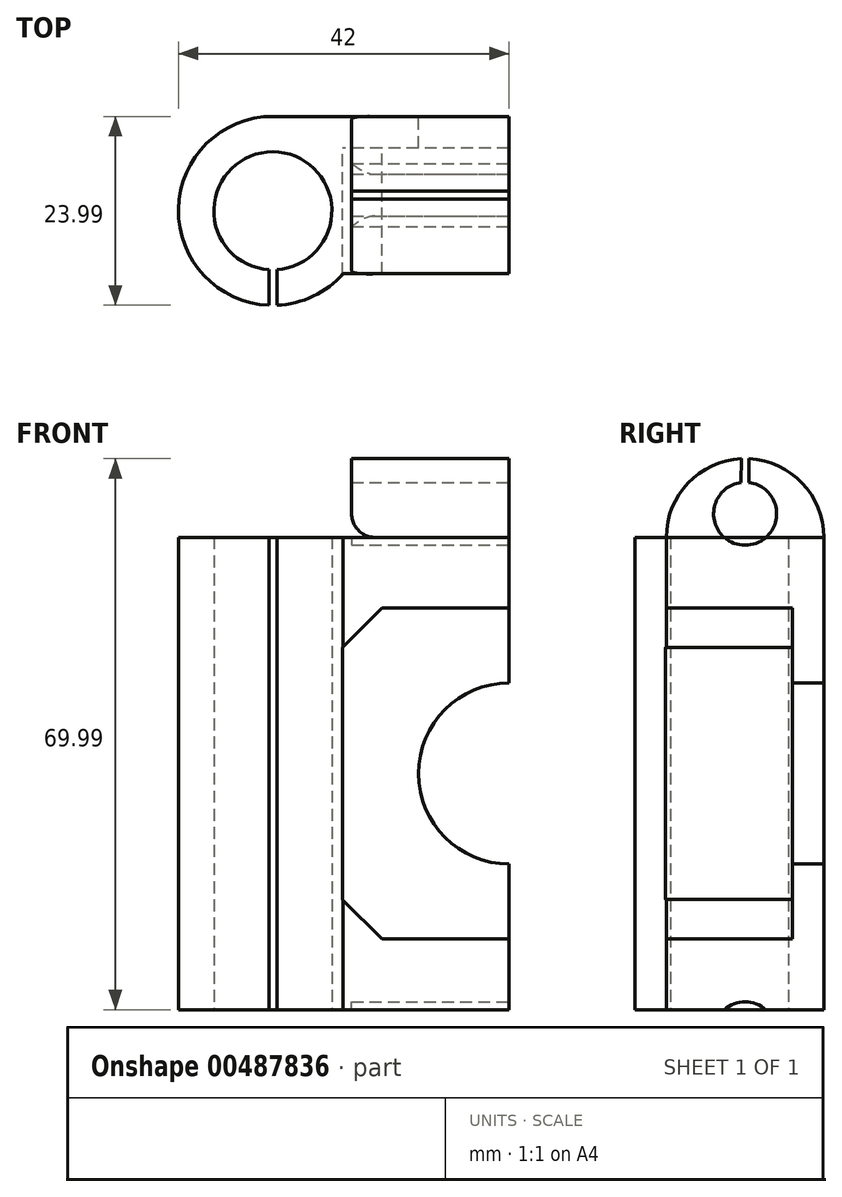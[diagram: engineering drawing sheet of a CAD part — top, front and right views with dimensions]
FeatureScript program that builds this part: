
annotation { "Feature Type Name" : "Feature", "Feature Type Description" : "" }
export const myFeature = defineFeature(function(context is Context, id is Id, definition is map)
    precondition{}
    {
        {
            var Q0;
            Q0=qCreatedBy(makeId("Top.planeOp"),FACE);
            var sketch = newSketch(context, id + "F0", { "sketchPlane" : qUnion([Q0])});
            skLineSegment(sketch, "E0.bottom", {"start": v(8.94, 0) * mm, "end": v(30, 0) * mm});
            skLineSegment(sketch, "E0.top", {"start": v(0, 20) * mm, "end": v(30, 20) * mm});
            skLineSegment(sketch, "E0.right", {"start": v(30, 0) * mm, "end": v(30, 20) * mm});
            skArc(sketch, "E1", {"start": v(0, 20) * mm, "mid": v(-10.95, 3.1) * mm, "end": v(8.94, 0) * mm});
            skCircle(sketch, "E2", {"center": v(0, 8) * mm, "radius": 7.5 * mm});
            skLineSegment(sketch, "E3", {"start": v(30, 0) * mm, "end": v(10, 0) * mm});
            skLineSegment(sketch, "E4", {"start": v(10, 0) * mm, "end": v(10, 20) * mm, "construction": true});
            skLineSegment(sketch, "E5.left", {"start": v(-0.5, -3.99) * mm, "end": v(-0.5, 0.52) * mm});
            skLineSegment(sketch, "E5.right", {"start": v(0.5, -3.99) * mm, "end": v(0.5, 0.52) * mm});
            skPoint(sketch, "E5.middle", {"position": v(0, 0) * mm});
            skPoint(sketch, "E6.orphan", {"position": v(-0.5, 4.29) * mm});
            skPoint(sketch, "E7.orphan", {"position": v(0.5, 4.29) * mm});
            skPoint(sketch, "E5.bottom.end.orphan", {"position": v(0.5, -4.29) * mm});
            skPoint(sketch, "E5.bottom.start.orphan", {"position": v(-0.5, -4.29) * mm});
            skSolve(sketch);
        }
        {
            var Q0;
            Q0=makeQuery(id+"F0.imprint","IMPRINT",FACE,{"disambiguationData":[TD([[makeQuery(id+"F0.imprint","IMPRINT",EDGE,{"derivedFrom":sQuery(id+"F0.wireOp",EDGE,"E0.bottom")}),1.0]])]});
            extrude(context, id + "F1", {"entities" : qUnion([Q0]), "depth" : 60 * mm, "offsetDistance" : 25 * mm, "symmetric" : true});
        }
        {
            var Q0;
            Q0=makeQuery(id+"F1.opExtrude","SWEPT_FACE",FACE,{"disambiguationData":[OSD([sQuery(id+"F0.wireOp",EDGE,"E0.top")])]});
            var sketch = newSketch(context, id + "F2", { "sketchPlane" : qUnion([Q0])});
            skLineSegment(sketch, "E8", {"start": v(-30, 30) * mm, "end": v(-30, 11.5) * mm});
            skLineSegment(sketch, "E9", {"start": v(-30, -30) * mm, "end": v(-30, -11.5) * mm});
            skArc(sketch, "E10", {"start": v(-30, -11.5) * mm, "mid": v(-18.5, 0) * mm, "end": v(-30, 11.5) * mm});
            skSolve(sketch);
        }
        {
            var Q0;
            {var subQ0=sQuery(id+"F2.wireOp",EDGE,"E10");Q0=makeQuery(id+"F2.imprint","IMPRINT",FACE,{"disambiguationData":[TD([[makeQuery(id+"F2.imprint","IMPRINT",EDGE,{"derivedFrom":subQ0}),1.0]])]});}
            extrude(context, id + "F3", {"entities" : qUnion([Q0]), "operationType" : NewBodyOperationType.REMOVE, "oppositeDirection" : true, "depth" : 25 * mm, "offsetDistance" : 25 * mm});
        }
        {
            var Q0;
            Q0=makeQuery(id+"F1.opExtrude","SWEPT_FACE",FACE,{"disambiguationData":[OSD([sQuery(id+"F0.wireOp",EDGE,"E0.top")])]});
            var sketch = newSketch(context, id + "F4", { "sketchPlane" : qUnion([Q0])});
            skLineSegment(sketch, "E11", {"start": v(-30, 21) * mm, "end": v(-13.85, 21) * mm});
            skLineSegment(sketch, "E12", {"start": v(-30, -21) * mm, "end": v(-13.85, -21) * mm});
            skLineSegment(sketch, "E13", {"start": v(-8.85, -16) * mm, "end": v(-8.85, 16) * mm});
            skLineSegment(sketch, "E14", {"start": v(-30, -21) * mm, "end": v(-30, 21) * mm});
            skPoint(sketch, "E15.visualSharp", {"position": v(-8.85, 21) * mm});
            skPoint(sketch, "E16.visualSharp", {"position": v(-8.85, -21) * mm});
            skLineSegment(sketch, "E17", {"start": v(-13.85, -21) * mm, "end": v(-8.85, -16) * mm});
            skLineSegment(sketch, "E18", {"start": v(-8.85, 16) * mm, "end": v(-13.85, 21) * mm});
            skLineSegment(sketch, "E19", {"start": v(-13.85, -21) * mm, "end": v(-8.85, -21) * mm, "construction": true});
            skLineSegment(sketch, "E20", {"start": v(-8.85, -16) * mm, "end": v(-8.85, -21) * mm, "construction": true});
            skLineSegment(sketch, "E21", {"start": v(-8.85, 16) * mm, "end": v(-8.85, 21) * mm, "construction": true});
            skLineSegment(sketch, "E22", {"start": v(-8.85, 21) * mm, "end": v(-13.85, 21) * mm, "construction": true});
            skSolve(sketch);
        }
        {
            var Q0;
            {var subQ3=sQuery(id+"F4.wireOp",EDGE,"E11");Q0=makeQuery(id+"F4.imprint","IMPRINT",FACE,{"disambiguationData":[TD([[makeQuery(id+"F4.imprint","IMPRINT",EDGE,{"derivedFrom":subQ3}),-1.0]])]});}
            extrude(context, id + "F5", {"entities" : qUnion([Q0]), "operationType" : NewBodyOperationType.REMOVE, "endBound" : BoundingType.THROUGH_ALL, "oppositeDirection" : true, "depth" : 10 * mm, "hasOffset" : true, "offsetDistance" : 10 * mm, "hasSecondDirection" : true, "secondDirectionOppositeDirection" : true, "secondDirectionDepth" : 4 * mm});
        }
        {
            var Q0;
            {var subQ0=sQuery(id+"F0.wireOp",EDGE,"E3");var subQ1=sQuery(id+"F0.wireOp",EDGE,"E0.right");var subQ2=sQuery(id+"F0.wireOp",EDGE,"E0.top");var subQ3=sQuery(id+"F0.wireOp",EDGE,"E0.bottom");Q0=makeQuery(id+"F3.boolean.opBoolean","SPLIT",FACE,{"disambiguationData":[TD([makeQuery(id+"F1.opExtrude","CAP_FACE",FACE,{"disambiguationData":[OSD([subQ3,subQ2,subQ1,sQuery(id+"F0.wireOp",EDGE,"E1"),sQuery(id+"F0.wireOp",EDGE,"E2"),subQ0])],"isStart":false})])],"derivedFrom":makeQuery(id+"F1.opExtrude","SWEPT_FACE",FACE,{"disambiguationData":[OSD([subQ1])]})});}
            var Q1;
            {var subQ0=sQuery(id+"F0.wireOp",EDGE,"E3");var subQ1=sQuery(id+"F0.wireOp",EDGE,"E0.right");var subQ2=sQuery(id+"F0.wireOp",EDGE,"E0.top");var subQ3=sQuery(id+"F0.wireOp",EDGE,"E0.bottom");Q1=makeQuery(id+"F3.boolean.opBoolean","SPLIT",FACE,{"disambiguationData":[TD([makeQuery(id+"F1.opExtrude","CAP_FACE",FACE,{"disambiguationData":[OSD([subQ3,subQ2,subQ1,sQuery(id+"F0.wireOp",EDGE,"E1"),sQuery(id+"F0.wireOp",EDGE,"E2"),subQ0])],"isStart":true})])],"derivedFrom":makeQuery(id+"F1.opExtrude","SWEPT_FACE",FACE,{"disambiguationData":[OSD([subQ1])]})});}
            cPlane(context, id + "F6", {"entities" : qUnion([Q0, Q1]), "cplaneType" : CPlaneType.MID_PLANE, "offset" : 25 * mm, "width" : 150 * mm, "height" : 150 * mm});
        }
        {
            var Q0;
            Q0=qCreatedBy(id+"F6.planeOp",FACE);
            var sketch = newSketch(context, id + "F7", { "sketchPlane" : qUnion([Q0])});
            skPoint(sketch, "E23", {"position": v(10, -30) * mm});
            skPoint(sketch, "E24", {"position": v(20, -30) * mm});
            skPoint(sketch, "E25", {"position": v(0, -30) * mm});
            skArc(sketch, "E26", {"start": v(20, -30) * mm, "mid": v(10, -40) * mm, "end": v(0, -30) * mm});
            skArc(sketch, "E27.MirrorCS", {"start": v(20, 30) * mm, "mid": v(10, 40) * mm, "end": v(0, 30) * mm});
            skLineSegment(sketch, "E28", {"start": v(20, 30) * mm, "end": v(0, 30) * mm});
            skLineSegment(sketch, "E29", {"start": v(20, -30) * mm, "end": v(0, -30) * mm});
            skSolve(sketch);
        }
        {
            var Q0;
            Q0=makeQuery(id+"F7.imprint","IMPRINT",FACE,{"disambiguationData":[TD([[makeQuery(id+"F7.imprint","IMPRINT",EDGE,{"derivedFrom":sQuery(id+"F7.wireOp",EDGE,"E27.MirrorCS")}),1.0]])]});
            var Q1;
            Q1=makeQuery(id+"F7.imprint","IMPRINT",FACE,{"disambiguationData":[TD([[makeQuery(id+"F7.imprint","IMPRINT",EDGE,{"derivedFrom":sQuery(id+"F7.wireOp",EDGE,"E26")}),-1.0]])]});
            extrude(context, id + "F8", {"entities" : qUnion([Q0, Q1]), "oppositeDirection" : true, "depth" : 20 * mm, "offsetDistance" : 25 * mm});
        }
        {
            var Q0;
            Q0=qCreatedBy(id+"F6.planeOp",FACE);
            var sketch = newSketch(context, id + "F9", { "sketchPlane" : qUnion([Q0])});
            skLineSegment(sketch, "E30", {"start": v(0, 0) * mm, "end": v(20, 0) * mm, "construction": true});
            skLineSegment(sketch, "E31", {"start": v(10, 0) * mm, "end": v(10, -39.9) * mm, "construction": true});
            skLineSegment(sketch, "E32", {"start": v(10, 0) * mm, "end": v(10, 40) * mm, "construction": true});
            skArc(sketch, "E33", {"start": v(9.5, 36.97) * mm, "mid": v(10, 29) * mm, "end": v(10.5, 36.97) * mm});
            skArc(sketch, "E34.MirrorC", {"start": v(9.5, -36.97) * mm, "mid": v(10, -29) * mm, "end": v(10.5, -36.97) * mm});
            skLineSegment(sketch, "E35.bottom", {"start": v(9.5, 40) * mm, "end": v(10.5, 40) * mm});
            skLineSegment(sketch, "E35.left", {"start": v(9.5, 40) * mm, "end": v(9.5, 36.97) * mm});
            skLineSegment(sketch, "E35.right", {"start": v(10.5, 40) * mm, "end": v(10.5, 36.97) * mm});
            skPoint(sketch, "E35.middle", {"position": v(10, 37) * mm});
            skPoint(sketch, "E36.orphan", {"position": v(9.5, 34) * mm});
            skPoint(sketch, "E35.top.end.orphan", {"position": v(10.5, 34) * mm});
            skLineSegment(sketch, "E37.MirrorCS", {"start": v(9.5, -40) * mm, "end": v(10.5, -40) * mm});
            skLineSegment(sketch, "E38.MirrorCS", {"start": v(10.5, -40) * mm, "end": v(10.5, -36.97) * mm});
            skLineSegment(sketch, "E39.MirrorCS", {"start": v(9.5, -40) * mm, "end": v(9.5, -36.97) * mm});
            skSolve(sketch);
        }
        {
            var Q0;
            Q0=makeQuery(id+"F9.imprint","IMPRINT",FACE,{"disambiguationData":[TD([[makeQuery(id+"F9.imprint","IMPRINT",EDGE,{"derivedFrom":sQuery(id+"F9.wireOp",EDGE,"E33")}),1.0]])]});
            var Q1;
            Q1=makeQuery(id+"F9.imprint","IMPRINT",FACE,{"disambiguationData":[TD([[makeQuery(id+"F9.imprint","IMPRINT",EDGE,{"derivedFrom":sQuery(id+"F9.wireOp",EDGE,"E34.MirrorC")}),-1.0]])]});
            var Q2;
            Q2=makeQuery(id+"F9.imprint","IMPRINT",FACE,{"disambiguationData":[TD([[makeQuery(id+"F9.imprint","IMPRINT",EDGE,{"derivedFrom":sQuery(id+"F9.wireOp",EDGE,"E35.bottom")}),-1.0]])]});
            var Q3;
            Q3=makeQuery(id+"F9.imprint","IMPRINT",FACE,{"disambiguationData":[TD([[makeQuery(id+"F9.imprint","IMPRINT",EDGE,{"derivedFrom":sQuery(id+"F9.wireOp",EDGE,"E37.MirrorCS")}),1.0]])]});
            extrude(context, id + "F10", {"entities" : qUnion([Q0, Q1, Q2, Q3]), "operationType" : NewBodyOperationType.REMOVE, "oppositeDirection" : true, "depth" : 20 * mm, "offsetDistance" : 25 * mm});
        }
        {
            var Q0;
            {var subQ0=sQuery(id+"F7.wireOp",EDGE,"E29");var subQ1=sQuery(id+"F7.wireOp",EDGE,"E26");var subQ2=makeQuery(id+"F8.opExtrude","CAP_FACE",FACE,{"disambiguationData":[OSD([subQ1,subQ0])],"isStart":false});var subQ3=sQuery(id+"F0.wireOp",EDGE,"E3");var subQ4=sQuery(id+"F0.wireOp",EDGE,"E0.bottom");var subQ5=makeQuery(id+"F1.opExtrude","CAP_FACE",FACE,{"disambiguationData":[OSD([subQ4,sQuery(id+"F0.wireOp",EDGE,"E0.top"),sQuery(id+"F0.wireOp",EDGE,"E0.right"),sQuery(id+"F0.wireOp",EDGE,"E1"),sQuery(id+"F0.wireOp",EDGE,"E2"),subQ3])],"isStart":true});Q0=makeQuery(id+"F10.boolean.opBoolean","SPLIT",EDGE,{"disambiguationData":[topologyDisambiguationEdgeConnected([subQ5,subQ2]),TD([makeQuery(id+"F1.opExtrude","SWEPT_FACE",FACE,{"disambiguationData":[OSD([subQ4,subQ3])]})])],"derivedFrom":makeQuery(id+"F8.opExtrude","CAP_EDGE",EDGE,{"disambiguationData":[OSD([subQ0])],"isStart":false})});}
            var Q1;
            {var subQ0=sQuery(id+"F7.wireOp",EDGE,"E29");var subQ1=sQuery(id+"F7.wireOp",EDGE,"E26");var subQ2=makeQuery(id+"F8.opExtrude","CAP_FACE",FACE,{"disambiguationData":[OSD([subQ1,subQ0])],"isStart":false});var subQ3=sQuery(id+"F0.wireOp",EDGE,"E0.top");var subQ5=makeQuery(id+"F1.opExtrude","CAP_FACE",FACE,{"disambiguationData":[OSD([sQuery(id+"F0.wireOp",EDGE,"E0.bottom"),subQ3,sQuery(id+"F0.wireOp",EDGE,"E0.right"),sQuery(id+"F0.wireOp",EDGE,"E1"),sQuery(id+"F0.wireOp",EDGE,"E2"),sQuery(id+"F0.wireOp",EDGE,"E3")])],"isStart":true});Q1=makeQuery(id+"F10.boolean.opBoolean","SPLIT",EDGE,{"disambiguationData":[topologyDisambiguationEdgeConnected([subQ5,subQ2]),TD([makeQuery(id+"F1.opExtrude","SWEPT_FACE",FACE,{"disambiguationData":[OSD([subQ3])]})])],"derivedFrom":makeQuery(id+"F8.opExtrude","CAP_EDGE",EDGE,{"disambiguationData":[OSD([subQ0])],"isStart":false})});}
            var Q2;
            {var subQ0=sQuery(id+"F7.wireOp",EDGE,"E28");var subQ1=sQuery(id+"F7.wireOp",EDGE,"E27.MirrorCS");var subQ2=makeQuery(id+"F8.opExtrude","CAP_FACE",FACE,{"disambiguationData":[OSD([subQ1,subQ0])],"isStart":false});var subQ4=sQuery(id+"F0.wireOp",EDGE,"E0.top");var subQ5=makeQuery(id+"F1.opExtrude","CAP_FACE",FACE,{"disambiguationData":[OSD([sQuery(id+"F0.wireOp",EDGE,"E0.bottom"),subQ4,sQuery(id+"F0.wireOp",EDGE,"E0.right"),sQuery(id+"F0.wireOp",EDGE,"E1"),sQuery(id+"F0.wireOp",EDGE,"E2"),sQuery(id+"F0.wireOp",EDGE,"E3")])],"isStart":false});Q2=makeQuery(id+"F10.boolean.opBoolean","SPLIT",EDGE,{"disambiguationData":[topologyDisambiguationEdgeConnected([subQ5,subQ2]),TD([makeQuery(id+"F1.opExtrude","SWEPT_FACE",FACE,{"disambiguationData":[OSD([subQ4])]})])],"derivedFrom":makeQuery(id+"F8.opExtrude","CAP_EDGE",EDGE,{"disambiguationData":[OSD([subQ0])],"isStart":false})});}
            var Q3;
            {var subQ0=sQuery(id+"F7.wireOp",EDGE,"E27.MirrorCS");var subQ1=sQuery(id+"F7.wireOp",EDGE,"E28");var subQ2=makeQuery(id+"F8.opExtrude","CAP_FACE",FACE,{"disambiguationData":[OSD([subQ0,subQ1])],"isStart":false});var subQ4=sQuery(id+"F0.wireOp",EDGE,"E3");var subQ5=sQuery(id+"F0.wireOp",EDGE,"E0.bottom");var subQ6=makeQuery(id+"F1.opExtrude","CAP_FACE",FACE,{"disambiguationData":[OSD([subQ5,sQuery(id+"F0.wireOp",EDGE,"E0.top"),sQuery(id+"F0.wireOp",EDGE,"E0.right"),sQuery(id+"F0.wireOp",EDGE,"E1"),sQuery(id+"F0.wireOp",EDGE,"E2"),subQ4])],"isStart":false});Q3=makeQuery(id+"F10.boolean.opBoolean","SPLIT",EDGE,{"disambiguationData":[topologyDisambiguationEdgeConnected([subQ6,subQ2]),TD([makeQuery(id+"F1.opExtrude","SWEPT_FACE",FACE,{"disambiguationData":[OSD([subQ5,subQ4])]})])],"derivedFrom":makeQuery(id+"F8.opExtrude","CAP_EDGE",EDGE,{"disambiguationData":[OSD([subQ1])],"isStart":false})});}
            fillet(context, id + "F11", {"entities" : qUnion([Q0, Q1, Q2, Q3]), "tangentPropagation" : true, "radius" : 3 * mm, "defaultsChanged" : false, "vertexSettings" : [], "allowEdgeOverflow" : false});
        }
    });
